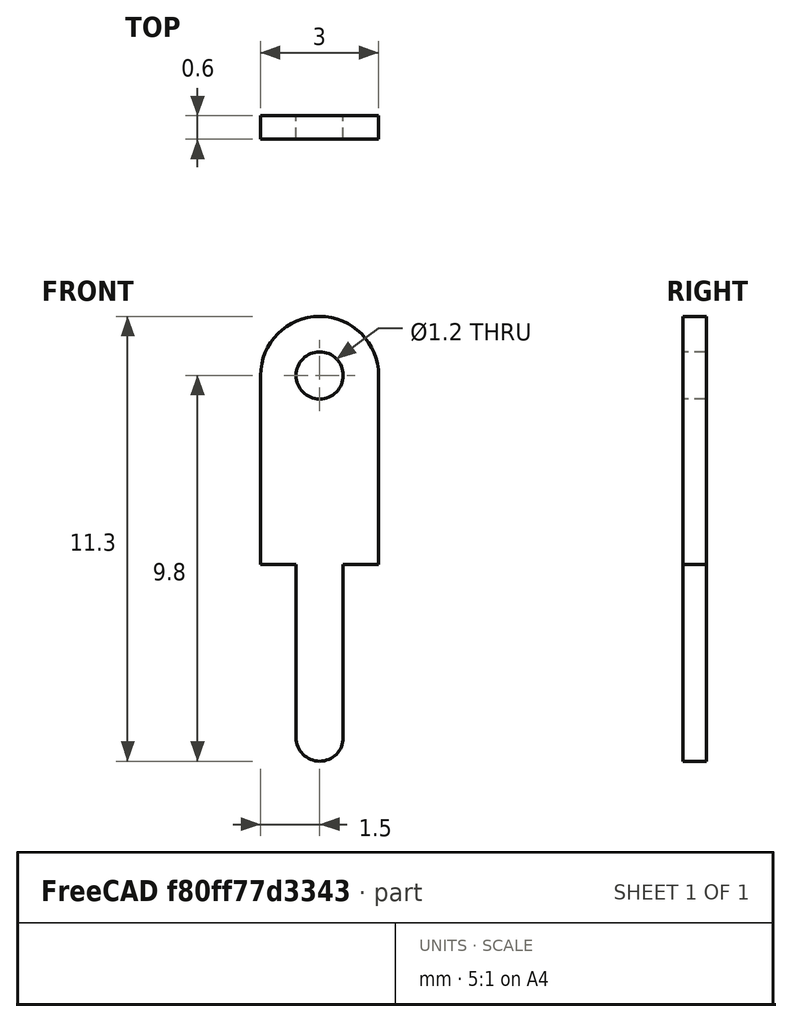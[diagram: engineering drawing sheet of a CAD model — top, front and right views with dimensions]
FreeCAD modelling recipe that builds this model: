
FCSTD DOCUMENT  (FreeCAD 0.17R12018 (Git))
Label: Pin_d1.2mm_L11.3mm_W3.0mm_Flat
License: All rights reserved
LicenseURL: http://en.wikipedia.org/wiki/All_rights_reserved
objects: Spreadsheet::Sheet×1, Sketcher::SketchObject×1, PartDesign::Pad×1, PartDesign::Body×1, App::Part×1
note: 4 computed .brp shape members not serialized (recipe doc carries the construction recipe); baked Part::Feature solids carry a one-line shape summary decoded from their .brp

FEATURE [Spreadsheet::Sheet] Spreadsheet  label="dimensions"
  cells = A1="L"; B1(L)=11.300000000000001; A2="Wtop"; B2(Wtop)=3; A3="Wbottom"; B3(Wbottom)=1.2; A4="Lbottom"; B4(Lbottom)=5; A5="Wfork"; B5(Wfork)=1.2; A7="thick"; B7(thick)=0.59999999999999998
FEATURE [Sketcher::SketchObject] Sketch
  MapMode = 5
  Placement = pos=(0,0,0) rot=(0,0.707107,0.707107;3.14159rad)
  Support = -> [XZ_Plane001]
  expr: Constraints[19] = dimensions.Lbottom - dimensions.Wbottom / 2
  expr: Constraints[21] = (dimensions.Wtop - dimensions.Wbottom) / 2
  expr: Constraints[20] = dimensions.Wbottom
  expr: Constraints[14] = dimensions.L - dimensions.Lbottom - dimensions.Wtop / 2
  expr: Constraints[22] = dimensions.Wtop
  expr: Constraints[25] = dimensions.Wfork / 2
  sketch-geometry (11):
    g0: LineSegment StartX=-1.5 StartY=4.8 StartZ=0 EndX=-1.5 EndY=0 EndZ=0
    g1: LineSegment StartX=-1.5 StartY=0 StartZ=0 EndX=-0.6 EndY=0 EndZ=0
    g2: LineSegment StartX=-0.6 StartY=0 StartZ=0 EndX=-0.6 EndY=-4.4 EndZ=0
    g3: LineSegment StartX=0.6 StartY=0 StartZ=0 EndX=0.6 EndY=-4.4 EndZ=0
    g4: LineSegment StartX=0.6 StartY=0 StartZ=0 EndX=1.5 EndY=0 EndZ=0
    g5: LineSegment StartX=1.5 StartY=0 StartZ=0 EndX=1.5 EndY=4.8 EndZ=0
    g6: ArcOfCircle CenterX=0 CenterY=-4.4 CenterZ=0 NormalX=0 NormalY=0 NormalZ=1 Radius=0.6 StartAngle=3.14159 EndAngle=6.28319
    g7: LineSegment [constr] StartX=-0.6 StartY=-4.4 StartZ=0 EndX=0.6 EndY=-4.4 EndZ=0
    g8: Circle CenterX=0 CenterY=4.8 CenterZ=0 NormalX=0 NormalY=0 NormalZ=1 Radius=0.6
    g9: ArcOfCircle CenterX=0 CenterY=4.8 CenterZ=0 NormalX=0 NormalY=0 NormalZ=1 Radius=1.5 StartAngle=0 EndAngle=3.14159
    g10: LineSegment [constr] StartX=-1.5 StartY=4.8 StartZ=0 EndX=1.5 EndY=4.8 EndZ=0
  constraints (34):
    c: PointOnObject(g3,g-1)
    c: PointOnObject(g6,g-2)
    c: Coincident(g7,g3)
    c: Coincident(g7,g2)
    c: Coincident(g2,g6)
    c: Coincident(g3,g6)
    c: PointOnObject(g6,g7)
    c: Horizontal(g7)
    c: Vertical(g3)
    c: Vertical(g2)
    c: Horizontal(g1)
    c: Horizontal(g4)
    c: Vertical(g5)
    c: Vertical(g0)
    c: DistanceY(g5,g5) = 4.8
    c: Coincident(g5,g4)
    c: Coincident(g0,g1)
    c: Coincident(g4,g3)
    c: Coincident(g1,g2)
    c: DistanceY(g3,g3) = 4.4
    c: DistanceX(g2,g3) = 1.2
    c: DistanceX(g1,g1) = 0.9
    c: DistanceX(g0,g5) = 3
    c: PointOnObject(g1,g-1)
    c: PointOnObject(g8,g-2)
    c: Radius(g8) = 0.6
    c: PointOnObject(g9,g-2)
    c: Coincident(g9,g0)
    c: Coincident(g9,g5)
    c: Coincident(g10,g0)
    c: Coincident(g10,g5)
    c: Horizontal(g10)
    c: PointOnObject(g9,g10)
    c: PointOnObject(g8,g10)
FEATURE [PartDesign::Pad] Pad  label="Pin_d1.2mm_L11.3mm_W3.0mm_Flat"
  Length = 0.6
  Length2 = 100
  Midplane = true
  Placement = pos=(0,0,0) rot=(1,0,0;1.5708rad)
  Profile = -> Sketch
  Type = 0
  expr: Length = dimensions.thick
FEATURE [PartDesign::Body] PadBody  label="Body"
  Group = -> [Sketch,Pad]
  Origin = -> Origin001
  Tip = -> Pad
FEATURE [App::Part] Part
  Group = -> [PadBody]
  License = CC BY 3.0
  LicenseURL = http://creativecommons.org/licenses/by/3.0/
  Origin = -> Origin
